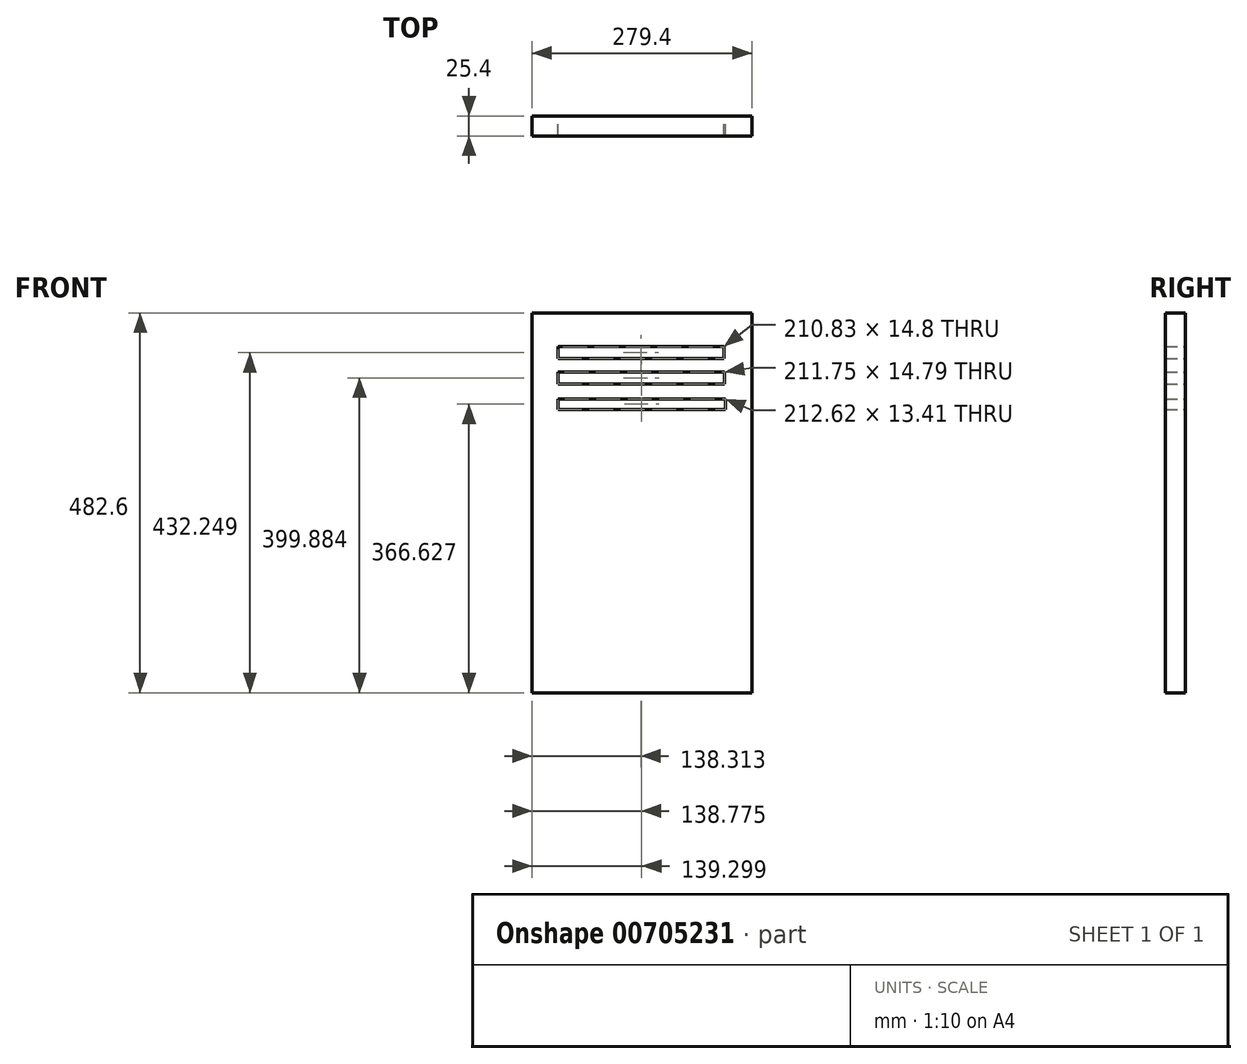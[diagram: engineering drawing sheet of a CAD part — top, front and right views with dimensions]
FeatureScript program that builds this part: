
annotation { "Feature Type Name" : "Feature", "Feature Type Description" : "" }
export const myFeature = defineFeature(function(context is Context, id is Id, definition is map)
    precondition{}
    {
        {
            var Q0;
            Q0=qCreatedBy(makeId("Front.planeOp"),FACE);
            var sketch = newSketch(context, id + "F0", { "sketchPlane" : qUnion([Q0])});
            skLineSegment(sketch, "E0.bottom", {"start": v(139.7, 241.3) * mm, "end": v(-139.7, 241.3) * mm});
            skLineSegment(sketch, "E0.top", {"start": v(139.7, -241.3) * mm, "end": v(-139.7, -241.3) * mm});
            skLineSegment(sketch, "E0.left", {"start": v(139.7, 241.3) * mm, "end": v(139.7, -241.3) * mm});
            skLineSegment(sketch, "E0.right", {"start": v(-139.7, 241.3) * mm, "end": v(-139.7, -241.3) * mm});
            skPoint(sketch, "E0.middle", {"position": v(0, 0) * mm});
            skSolve(sketch);
        }
        {
            var Q0;
            Q0=makeQuery(id+"F0.imprint","IMPRINT",FACE,{"disambiguationData":[TD([[makeQuery(id+"F0.imprint","IMPRINT",EDGE,{"derivedFrom":sQuery(id+"F0.wireOp",EDGE,"E0.bottom")}),1.0]])]});
            var sketch = newSketch(context, id + "F1", { "sketchPlane" : qUnion([Q0])});
            skLineSegment(sketch, "E1.bottom", {"start": v(-106.8, 198.35) * mm, "end": v(104.03, 198.35) * mm});
            skLineSegment(sketch, "E1.top", {"start": v(-106.8, 183.55) * mm, "end": v(104.03, 183.55) * mm});
            skLineSegment(sketch, "E1.left", {"start": v(-106.8, 198.35) * mm, "end": v(-106.8, 183.55) * mm});
            skLineSegment(sketch, "E1.right", {"start": v(104.03, 198.35) * mm, "end": v(104.03, 183.55) * mm});
            skLineSegment(sketch, "E2.bottom", {"start": v(-106.8, 165.98) * mm, "end": v(104.95, 165.98) * mm});
            skLineSegment(sketch, "E2.top", {"start": v(-106.8, 151.19) * mm, "end": v(104.95, 151.19) * mm});
            skLineSegment(sketch, "E2.left", {"start": v(-106.8, 165.98) * mm, "end": v(-106.8, 151.19) * mm});
            skLineSegment(sketch, "E2.right", {"start": v(104.95, 165.98) * mm, "end": v(104.95, 151.19) * mm});
            skLineSegment(sketch, "E3.bottom", {"start": v(-106.71, 132.03) * mm, "end": v(105.91, 132.03) * mm});
            skLineSegment(sketch, "E3.top", {"start": v(-106.71, 118.62) * mm, "end": v(105.91, 118.62) * mm});
            skLineSegment(sketch, "E3.left", {"start": v(-106.71, 132.03) * mm, "end": v(-106.71, 118.62) * mm});
            skLineSegment(sketch, "E3.right", {"start": v(105.91, 132.03) * mm, "end": v(105.91, 118.62) * mm});
            skSolve(sketch);
        }
        {
            var Q0;
            Q0=makeQuery(id+"F1.imprint","IMPRINT",FACE,{"disambiguationData":[TD([[makeQuery(id+"F1.imprint","IMPRINT",EDGE,{"derivedFrom":sQuery(id+"F1.wireOp",EDGE,"E1.bottom")}),1.0]])]});
            extrude(context, id + "F2", {"entities" : qUnion([Q0]), "depth" : 25.4 * mm, "offsetDistance" : 25.4 * mm});
        }
    });
